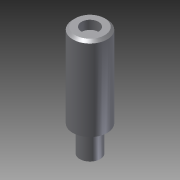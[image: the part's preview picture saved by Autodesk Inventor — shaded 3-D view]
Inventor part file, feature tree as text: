
AUTODESK INVENTOR PART (.ipt)
format: ipt  version: 2011 SP1 (Build 150282100, 282)  size: 105,984 bytes
history: native  units: in
note: dims shown in document units (in); Inventor stores cm internally (conversion verified against a paired STEP export)
features: other x49, revolve x1, sketch x1
ambient origin geometry x8: Origin, YZ Plane, XZ Plane, XY Plane, X Axis, Y Axis, Z Axis, Center Point
bodies: Solid1 (feature_tree)
feature tree (51):
  revolve  "Revolution1"  [1 undecoded]
  other  "paddle_to_bracket_XY"
  other  "paddle_to_bracket_YZ"
  other  "paddle_to_bracket_ZX"
  other  "paddle_to_bracket_X"
  other  "paddle_to_bracket_Y"
  other  "paddle_to_bracket_Z"
  other  "paddle_to_bracket_Center"
  other  "paddle_to_led_XY"
  other  "paddle_to_led_YZ"
  other  "paddle_to_led_ZX"
  other  "paddle_to_led_X"
  other  "paddle_to_led_Y"
  other  "paddle_to_led_Z"
  other  "paddle_to_led_Center"
  other  "paddle_to_led_green_XY"
  other  "paddle_to_led_green_YZ"
  other  "paddle_to_led_green_ZX"
  other  "paddle_to_led_green_X"
  other  "paddle_to_led_green_Y"
  other  "paddle_to_led_green_Z"
  other  "paddle_to_led_green_Center"
  other  "rocker_to_bracket_XY"
  other  "rocker_to_bracket_YZ"
  other  "rocker_to_bracket_ZX"
  other  "rocker_to_bracket_X"
  other  "rocker_to_bracket_Y"
  other  "rocker_to_bracket_Z"
  other  "rocker_to_bracket_Center"
  other  "toggle_to_bc_XY"
  other  "toggle_to_bc_YZ"
  other  "toggle_to_bc_ZX"
  other  "toggle_to_bc_X"
  other  "toggle_to_bc_Y"
  other  "toggle_to_bc_Z"
  other  "toggle_to_bc_Center"
  other  "toggle_to_led_XY"
  other  "toggle_to_led_YZ"
  other  "toggle_to_led_ZX"
  other  "toggle_to_led_X"
  other  "toggle_to_led_Y"
  other  "toggle_to_led_Z"
  other  "toggle_to_led_Center"
  other  "toggle_to_led_green_XY"
  other  "toggle_to_led_green_YZ"
  other  "toggle_to_led_green_ZX"
  other  "toggle_to_led_green_X"
  other  "toggle_to_led_green_Y"
  other  "toggle_to_led_green_Z"
  other  "toggle_to_led_green_Center"
  sketch  "Sketch_1"  dims[d0=360.0deg]
note: 1 required parameter value undecoded (feature->parameter linkage not recoverable at this tier; creation-order binding heuristic only, values carry confidence <= 0.55)
